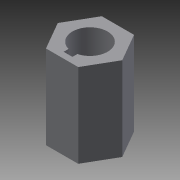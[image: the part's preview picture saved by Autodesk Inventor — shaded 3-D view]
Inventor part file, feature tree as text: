
AUTODESK INVENTOR PART (.ipt)
format: ipt  version: 2013 (Build 170138000, 138)  size: 79,872 bytes
history: native  units: in
note: dims shown in document units (in); Inventor stores cm internally (conversion verified against a paired STEP export)
features: extrude x1, sketch x1
ambient origin geometry x8: Origin, YZ Plane, XZ Plane, XY Plane, X Axis, Y Axis, Z Axis, Center Point
bodies: Solid1 (feature_tree)
feature tree (2):
  extrude  "Extrusion1"  Depth=0.315in
  sketch  "Sketch1"  dims[d0=0.5in d1=0.315in d2=0.0787in d3=0.0394in d4=0.1969in d5=0.75in d6=0.0in]
